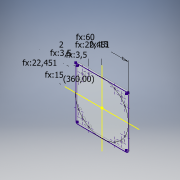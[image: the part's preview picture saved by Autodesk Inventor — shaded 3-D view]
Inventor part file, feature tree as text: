
AUTODESK INVENTOR PART (.ipt)
format: ipt  version: 2019 (Build 230136000, 136)  size: 148,992 bytes
history: native  units: mm
features: hole x2, other x1, sketch x1, extrude x1
ambient origin geometry x8: Origin, YZ Plane, XZ Plane, XY Plane, X Axis, Y Axis, Z Axis, Center Point
bodies: Solid1 (feature_tree)
feature tree (5):
  other  "<userpath>\OneDrive - Van Ierland\Documents\Inventor\FlightSim\Instrument.xlsx"
  sketch  "Sketch1"  dims[d0=60.0mm d1=2.0mm d2=22.45064mm d3=22.45064mm d4=15.0mm d5=15.0mm d6=3.5mm d7=3.5mm d8=40.0mm d10=360.0deg d12=2.0mm d13=0.0mm d14=3.4mm d15=6.0mm d16=6.3mm d17=2.0mm d18=90.0deg d19=8.0mm d20=20.594885mm d21=2.4mm d22=6.0mm d23=4.4mm d24=2.0mm d25=90.0deg d26=8.0mm d27=20.594885mm]
  extrude  "Extrusion1"  Depth=2.0mm
  hole  "Hole1"  [1 undecoded]
  hole  "Hole2"  [1 undecoded]
note: 2 required parameter values undecoded (feature->parameter linkage not recoverable at this tier; creation-order binding heuristic only, values carry confidence <= 0.55)
